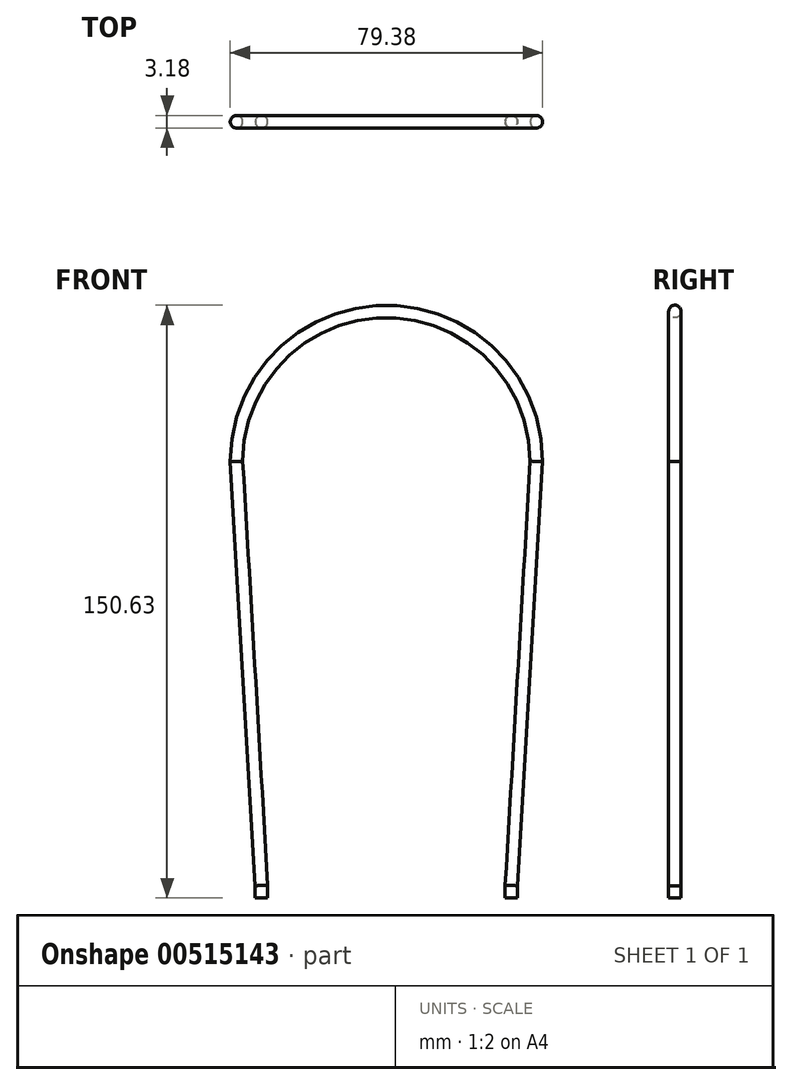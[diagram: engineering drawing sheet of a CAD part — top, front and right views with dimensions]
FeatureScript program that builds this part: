
annotation { "Feature Type Name" : "Feature", "Feature Type Description" : "" }
export const myFeature = defineFeature(function(context is Context, id is Id, definition is map)
    precondition{}
    {
        {
            var Q0;
            Q0=qCreatedBy(makeId("Front.planeOp"),FACE);
            var sketch = newSketch(context, id + "F0", { "sketchPlane" : qUnion([Q0])});
            skPoint(sketch, "E0.start.orphan", {"position": v(0, 0) * mm});
            skLineSegment(sketch, "E1", {"start": v(0, 0) * mm, "end": v(0, 3.18) * mm});
            skLineSegment(sketch, "E2", {"start": v(0, 3.18) * mm, "end": v(-6.35, 110.94) * mm});
            skLineSegment(sketch, "E3", {"start": v(69.85, 110.94) * mm, "end": v(63.5, 3.17) * mm});
            skLineSegment(sketch, "E4", {"start": v(63.5, 3.18) * mm, "end": v(63.5, 0) * mm});
            skArc(sketch, "E5", {"start": v(69.85, 110.94) * mm, "mid": v(31.75, 149.04) * mm, "end": v(-6.35, 110.94) * mm});
            skSolve(sketch);
        }
        {
            var Q0;
            Q0=qCreatedBy(makeId("Top.planeOp"),FACE);
            var sketch = newSketch(context, id + "F1", { "sketchPlane" : qUnion([Q0])});
            skCircle(sketch, "E6", {"center": v(0, 0) * mm, "radius": 1.59 * mm});
            skSolve(sketch);
        }
        {
            var Q0;
            Q0=makeQuery(id+"F1.imprint","IMPRINT",FACE,{"disambiguationData":[TD([[makeQuery(id+"F1.imprint","IMPRINT",EDGE,{"derivedFrom":sQuery(id+"F1.wireOp",EDGE,"E6")}),1.0]])]});
            var Q1;
            Q1=sQuery(id+"F0.wireOp",EDGE,"E1");
            var Q2;
            Q2=sQuery(id+"F0.wireOp",EDGE,"E2");
            var Q3;
            Q3=sQuery(id+"F0.wireOp",EDGE,"E5");
            var Q4;
            Q4=sQuery(id+"F0.wireOp",EDGE,"E3");
            var Q5;
            Q5=sQuery(id+"F0.wireOp",EDGE,"E4");
            sweep(context, id + "F2", {"profiles" : qUnion([Q0]), "path" : qUnion([Q1, Q2, Q3, Q4, Q5])});
        }
    });
